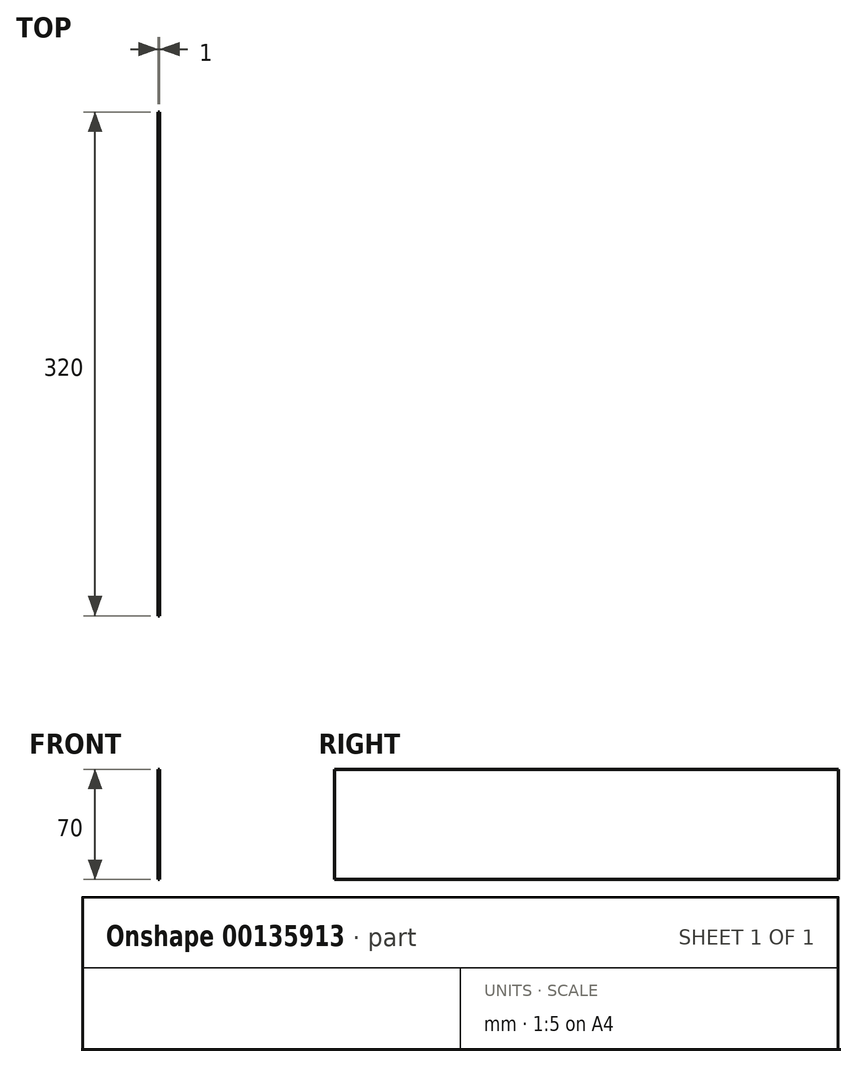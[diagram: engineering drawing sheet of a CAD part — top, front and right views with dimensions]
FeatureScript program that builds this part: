
annotation { "Feature Type Name" : "Feature", "Feature Type Description" : "" }
export const myFeature = defineFeature(function(context is Context, id is Id, definition is map)
    precondition{}
    {
        {
            var Q0;
            Q0=qCreatedBy(makeId("Right.planeOp"),FACE);
            var sketch = newSketch(context, id + "F0", { "sketchPlane" : qUnion([Q0])});
            skLineSegment(sketch, "E0.bottom", {"start": v(-54.34, 0) * mm, "end": v(265.66, 0) * mm});
            skLineSegment(sketch, "E0.top", {"start": v(-54.34, 70) * mm, "end": v(265.66, 70) * mm});
            skLineSegment(sketch, "E0.left", {"start": v(-54.34, 0) * mm, "end": v(-54.34, 70) * mm});
            skLineSegment(sketch, "E0.right", {"start": v(265.66, 0) * mm, "end": v(265.66, 70) * mm});
            skSolve(sketch);
        }
        {
            var Q0;
            Q0 = qSketchRegion(id + "F0", true);
            extrude(context, id + "F1", {"entities" : qUnion([Q0]), "depth" : 1 * mm});
        }
    });
